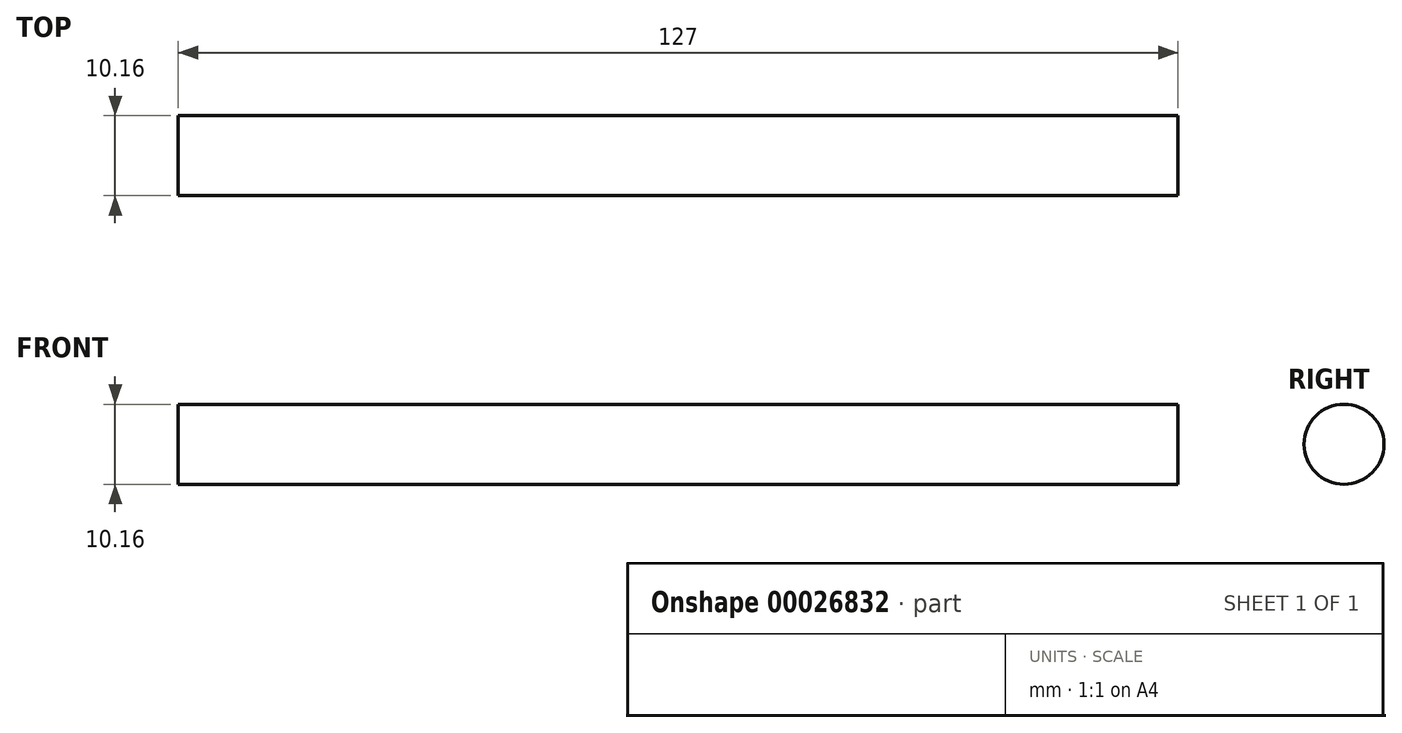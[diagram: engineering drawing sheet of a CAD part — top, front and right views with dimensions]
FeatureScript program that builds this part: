
annotation { "Feature Type Name" : "Feature", "Feature Type Description" : "" }
export const myFeature = defineFeature(function(context is Context, id is Id, definition is map)
    precondition{}
    {
        {
            var Q0;
            Q0=qCreatedBy(makeId("Right.planeOp"),FACE);
            var sketch = newSketch(context, id + "F0", { "sketchPlane" : qUnion([Q0])});
            skCircle(sketch, "E0", {"center": v(0, 0) * mm, "radius": 5.08 * mm});
            skSolve(sketch);
        }
        {
            var Q0;
            Q0=makeQuery(id+"F0.imprint","IMPRINT",FACE,{"disambiguationData":[TD([[makeQuery(id+"F0.imprint","IMPRINT",EDGE,{"derivedFrom":sQuery(id+"F0.wireOp",EDGE,"E0")}),1.0]])]});
            extrude(context, id + "F1", {"entities" : qUnion([Q0]), "endBound" : BoundingType.SYMMETRIC, "depth" : 127 * mm});
        }
    });
